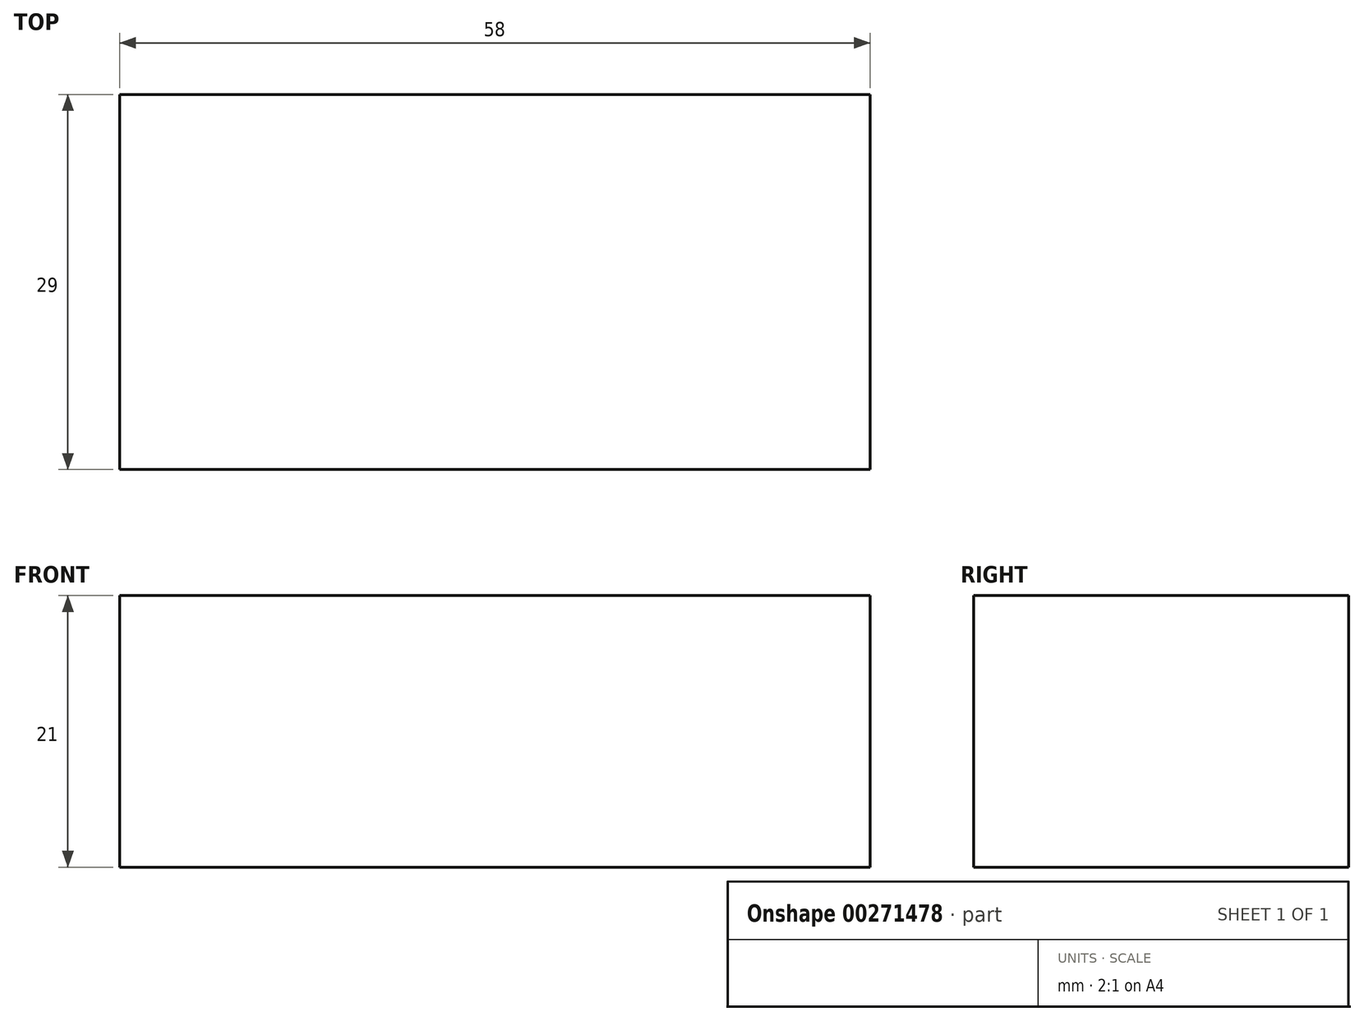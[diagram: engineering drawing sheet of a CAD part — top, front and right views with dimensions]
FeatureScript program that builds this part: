
annotation { "Feature Type Name" : "Feature", "Feature Type Description" : "" }
export const myFeature = defineFeature(function(context is Context, id is Id, definition is map)
    precondition{}
    {
        {
            var Q0;
            Q0=qCreatedBy(makeId("Top.planeOp"),FACE);
            var sketch = newSketch(context, id + "F0", { "sketchPlane" : qUnion([Q0])});
            skLineSegment(sketch, "E0.bottom", {"start": v(0, 0) * mm, "end": v(58, 0) * mm});
            skLineSegment(sketch, "E0.top", {"start": v(0, 29) * mm, "end": v(58, 29) * mm});
            skLineSegment(sketch, "E0.left", {"start": v(0, 0) * mm, "end": v(0, 29) * mm});
            skLineSegment(sketch, "E0.right", {"start": v(58, 0) * mm, "end": v(58, 29) * mm});
            skSolve(sketch);
        }
        {
            var Q0;
            Q0=makeQuery(id+"F0.imprint","IMPRINT",FACE,{"disambiguationData":[TD([[makeQuery(id+"F0.imprint","IMPRINT",EDGE,{"derivedFrom":sQuery(id+"F0.wireOp",EDGE,"E0.bottom")}),1.0]])]});
            extrude(context, id + "F1", {"entities" : qUnion([Q0]), "depth" : 21 * mm});
        }
    });
